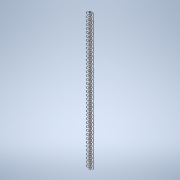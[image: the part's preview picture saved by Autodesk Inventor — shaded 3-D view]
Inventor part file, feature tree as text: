
AUTODESK INVENTOR PART (.ipt)
format: ipt  version: 2020 (Build 240168000, 168)  size: 510,464 bytes
history: native  units: mm
features: sketch x3, extrude x2, helix x1, pattern_linear x1
ambient origin geometry x8: Origin, YZ Plane, XZ Plane, XY Plane, X Axis, Y Axis, Z Axis, Center Point
bodies: Solid1 (feature_tree)
feature tree (7):
  extrude  "Extrusion1"  Depth=800.0mm TaperAngle=0.0deg
  helix  "Coil1"  [1 undecoded]
  extrude  "Extrusion2"  Depth=2.0mm
  pattern_linear  "Rectangular Pattern1"  Spacing1=2.0mm  [1 undecoded]
  sketch  "Sketch1"  dims[d0=10.0mm d1=800.0mm d2=0.0mm d3=2.0mm]
  sketch  "Sketch2"  dims[d4=10.0mm d5=2.0mm]
  sketch  "Sketch3"  dims[d6=20.0mm d7=10.0mm d8=400.0mm d9=0.0mm d10=90.0deg d11=90.0deg d12=0.0mm d13=0.0mm d14=2.0mm d15=30.0deg d16=160.0mm d18=20.0mm]
note: 2 required parameter values undecoded (feature->parameter linkage not recoverable at this tier; creation-order binding heuristic only, values carry confidence <= 0.55)
